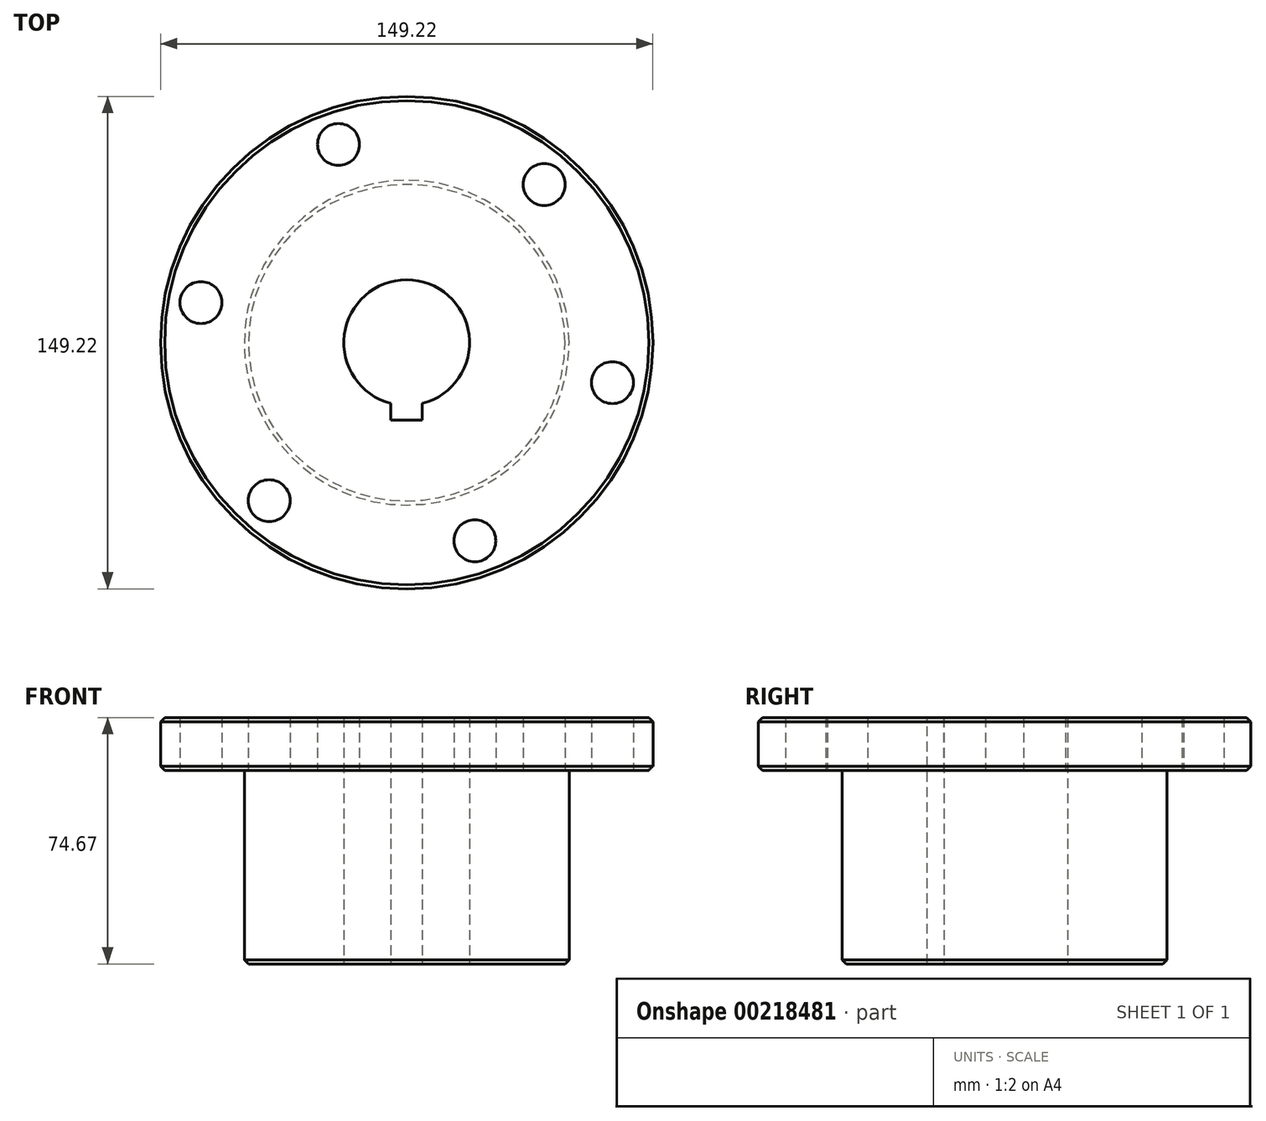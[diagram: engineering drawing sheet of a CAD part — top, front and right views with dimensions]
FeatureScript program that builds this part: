
annotation { "Feature Type Name" : "Feature", "Feature Type Description" : "" }
export const myFeature = defineFeature(function(context is Context, id is Id, definition is map)
    precondition{}
    {
        {
            var Q0;
            Q0=qCreatedBy(makeId("Top.planeOp"),FACE);
            var sketch = newSketch(context, id + "F0", { "sketchPlane" : qUnion([Q0])});
            skCircle(sketch, "E0", {"center": v(0, 0) * mm, "radius": 74.61 * mm});
            skSolve(sketch);
        }
        {
            var Q0;
            Q0 = qSketchRegion(id + "F0", true);
            extrude(context, id + "F1", {"entities" : qUnion([Q0]), "depth" : 16 * mm});
        }
        {
            var Q0;
            Q0=makeQuery(id+"F1.opExtrude","CAP_FACE",FACE,{"disambiguationData":[OSD([sQuery(id+"F0.wireOp",EDGE,"E0")])],"isStart":true});
            var sketch = newSketch(context, id + "F2", { "sketchPlane" : qUnion([Q0])});
            skCircle(sketch, "E1", {"center": v(0, 0) * mm, "radius": 49.21 * mm});
            skSolve(sketch);
        }
        {
            var Q0;
            Q0 = qSketchRegion(id + "F2", true);
            extrude(context, id + "F3", {"entities" : qUnion([Q0]), "operationType" : NewBodyOperationType.ADD, "depth" : 58.67 * mm});
        }
        {
            var Q0;
            Q0=makeQuery(id+"F3.opExtrude","CAP_FACE",FACE,{"disambiguationData":[OSD([sQuery(id+"F2.wireOp",EDGE,"E1")])],"isStart":false});
            var sketch = newSketch(context, id + "F4", { "sketchPlane" : qUnion([Q0])});
            skCircle(sketch, "E2", {"center": v(0, 0) * mm, "radius": 19.05 * mm});
            skSolve(sketch);
        }
        {
            var Q0;
            Q0 = qSketchRegion(id + "F4", true);
            extrude(context, id + "F5", {"entities" : qUnion([Q0]), "operationType" : NewBodyOperationType.REMOVE, "endBound" : BoundingType.THROUGH_ALL, "oppositeDirection" : true, "depth" : 25.4 * mm});
        }
        {
            var Q0;
            Q0=makeQuery(id+"F3.opExtrude","CAP_EDGE",EDGE,{"disambiguationData":[OSD([sQuery(id+"F2.wireOp",EDGE,"E1")])],"isStart":false});
            var Q1;
            Q1=makeQuery(id+"F1.opExtrude","CAP_EDGE",EDGE,{"disambiguationData":[OSD([sQuery(id+"F0.wireOp",EDGE,"E0")])],"isStart":true});
            var Q2;
            Q2=makeQuery(id+"F1.opExtrude","CAP_EDGE",EDGE,{"disambiguationData":[OSD([sQuery(id+"F0.wireOp",EDGE,"E0")])],"isStart":false});
            chamfer(context, id + "F6", {"entities" : qUnion([Q0, Q1, Q2]), "width" : 1.27 * mm, "tangentPropagation" : true});
        }
        {
            var Q0;
            Q0=makeQuery(id+"F1.opExtrude","CAP_FACE",FACE,{"disambiguationData":[OSD([sQuery(id+"F0.wireOp",EDGE,"E0")])],"isStart":true});
            var sketch = newSketch(context, id + "F7", { "sketchPlane" : qUnion([Q0])});
            skPoint(sketch, "E3", {"position": v(20.66, 60.04) * mm});
            skPoint(sketch, "E4.1.0", {"position": v(-41.67, 47.92) * mm});
            skPoint(sketch, "E4.2.0", {"position": v(-62.33, -12.13) * mm});
            skPoint(sketch, "E4.3.0", {"position": v(-20.66, -60.04) * mm});
            skPoint(sketch, "E4.4.0", {"position": v(41.67, -47.92) * mm});
            skPoint(sketch, "E4.5.0", {"position": v(62.33, 12.13) * mm});
            skPoint(sketch, "E4.center", {"position": v(0, 0) * mm});
            skSolve(sketch);
        }
        {
            var Q0;
            Q0=sQuery(id+"F7.wireOp",VERTEX,"E4.1.0");
            var Q1;
            Q1=sQuery(id+"F7.wireOp",VERTEX,"E3");
            var Q2;
            Q2=sQuery(id+"F7.wireOp",VERTEX,"E4.5.0");
            var Q3;
            Q3=sQuery(id+"F7.wireOp",VERTEX,"E4.4.0");
            var Q4;
            Q4=sQuery(id+"F7.wireOp",VERTEX,"E4.3.0");
            var Q5;
            Q5=sQuery(id+"F7.wireOp",VERTEX,"E4.2.0");
            var Q6;
            Q6=makeQuery(id+"F1.opExtrude","SWEPT_BODY",BODY,{"disambiguationData":[OSD([sQuery(id+"F0.wireOp",EDGE,"E0")])]});
            hole(context, id + "F8", {"style" : HoleStyle.SIMPLE, "endStyle" : HoleEndStyle.BLIND, "holeDiameter" : 12.7 * mm, "holeDepth" : 19.05 * mm, "startFromSketch" : true, "locations" : qUnion([Q0, Q1, Q2, Q3, Q4, Q5]), "scope" : qUnion([Q6])});
        }
        {
            var Q0;
            Q0=makeQuery(id+"F1.opExtrude","CAP_FACE",FACE,{"disambiguationData":[OSD([sQuery(id+"F0.wireOp",EDGE,"E0")])],"isStart":false});
            var sketch = newSketch(context, id + "F9", { "sketchPlane" : qUnion([Q0])});
            skLineSegment(sketch, "E5.bottom", {"start": v(4.76, -23.5) * mm, "end": v(-4.76, -23.5) * mm});
            skLineSegment(sketch, "E5.top", {"start": v(4.76, 4.44) * mm, "end": v(-4.76, 4.44) * mm});
            skLineSegment(sketch, "E5.left", {"start": v(4.76, -23.5) * mm, "end": v(4.76, 4.44) * mm});
            skLineSegment(sketch, "E5.right", {"start": v(-4.76, -23.5) * mm, "end": v(-4.76, 4.44) * mm});
            skPoint(sketch, "E5.middle", {"position": v(0, -9.53) * mm});
            skSolve(sketch);
        }
        {
            var Q0;
            Q0 = qSketchRegion(id + "F9", true);
            extrude(context, id + "F10", {"entities" : qUnion([Q0]), "operationType" : NewBodyOperationType.REMOVE, "endBound" : BoundingType.THROUGH_ALL, "oppositeDirection" : true, "depth" : 25.4 * mm, "offsetDistance" : 25.4 * mm});
        }
    });
